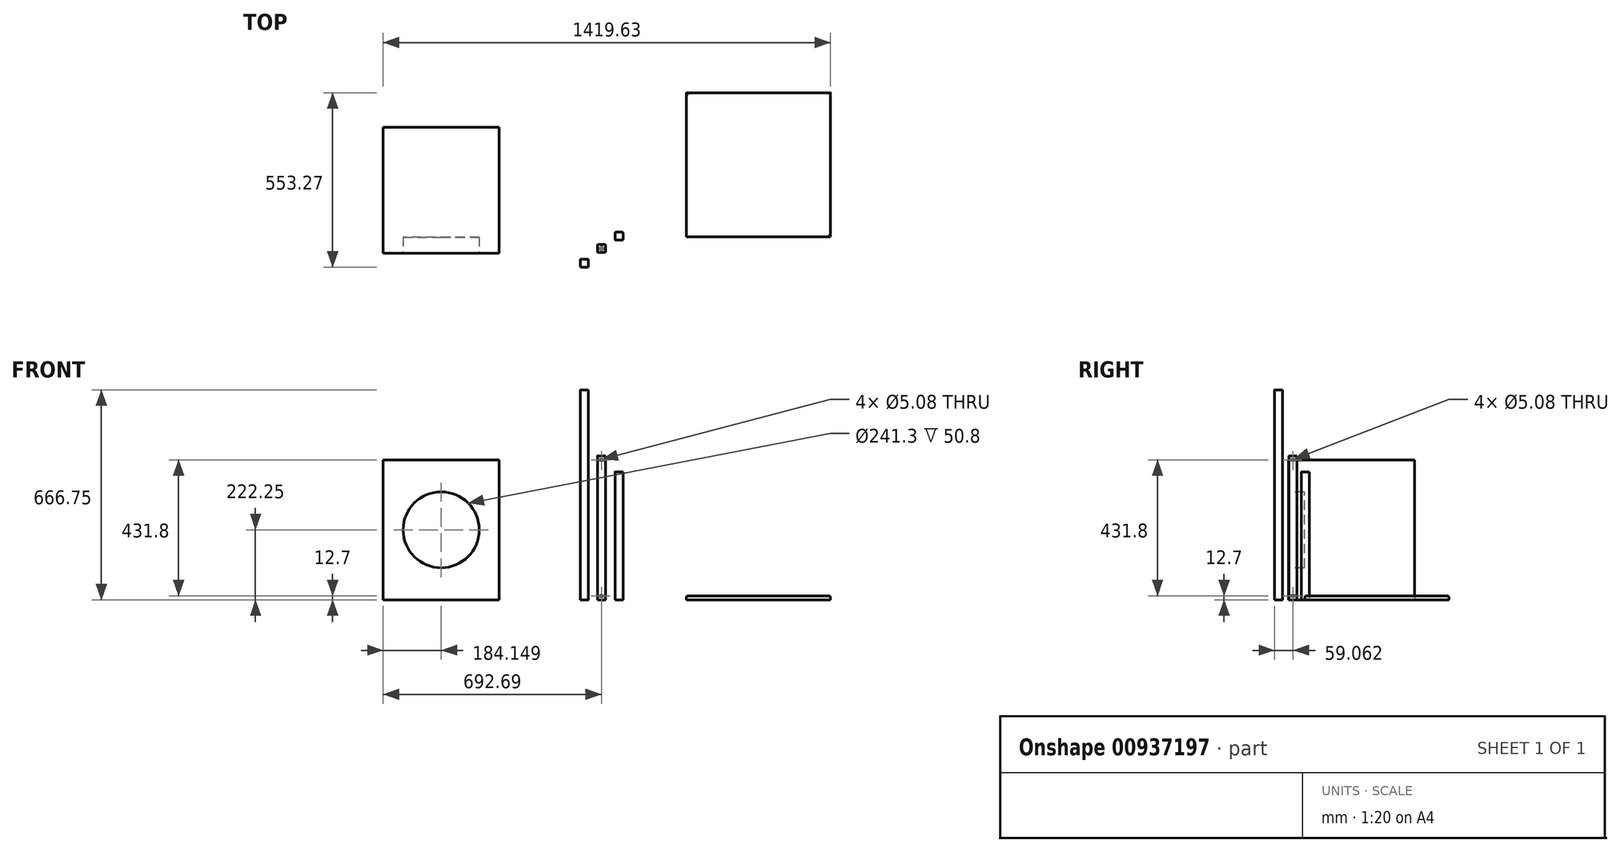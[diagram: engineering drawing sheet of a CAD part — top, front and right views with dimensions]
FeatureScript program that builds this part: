
annotation { "Feature Type Name" : "Feature", "Feature Type Description" : "" }
export const myFeature = defineFeature(function(context is Context, id is Id, definition is map)
    precondition{}
    {
        {
            var Q0;
            Q0=qCreatedBy(makeId("Top.planeOp"),FACE);
            var sketch = newSketch(context, id + "F0", { "sketchPlane" : qUnion([Q0])});
            skLineSegment(sketch, "E0.bottom", {"start": v(-525.27, 322.35) * mm, "end": v(-156.97, 322.35) * mm});
            skLineSegment(sketch, "E0.top", {"start": v(-525.27, -77.7) * mm, "end": v(-156.97, -77.7) * mm});
            skLineSegment(sketch, "E0.left", {"start": v(-525.27, 322.35) * mm, "end": v(-525.27, -77.7) * mm});
            skLineSegment(sketch, "E0.right", {"start": v(-156.97, 322.35) * mm, "end": v(-156.97, -77.7) * mm});
            skSolve(sketch);
        }
        {
            var Q0;
            Q0 = qSketchRegion(id + "F0", true);
            extrude(context, id + "F1", {"entities" : qUnion([Q0]), "depth" : 444.5 * mm, "offsetDistance" : 25.4 * mm});
        }
        {
            var Q0;
            Q0=makeQuery(id+"F1.opExtrude","SWEPT_FACE",FACE,{"disambiguationData":[OSD([sQuery(id+"F0.wireOp",EDGE,"E0.top")])]});
            var sketch = newSketch(context, id + "F2", { "sketchPlane" : qUnion([Q0])});
            skLineSegment(sketch, "E1", {"start": v(-341.12, 0) * mm, "end": v(-341.12, 222.25) * mm, "construction": true});
            skPoint(sketch, "E1.endSnap0", {"position": v(-525.27, 222.25) * mm});
            skCircle(sketch, "E2", {"center": v(-341.12, 222.25) * mm, "radius": 120.65 * mm});
            skSolve(sketch);
        }
        {
            var Q0;
            Q0 = qSketchRegion(id + "F2", true);
            extrude(context, id + "F3", {"entities" : qUnion([Q0]), "operationType" : NewBodyOperationType.REMOVE, "oppositeDirection" : true, "depth" : 50.8 * mm, "offsetDistance" : 25.4 * mm});
        }
        {
            var Q0;
            Q0=qCreatedBy(makeId("Top.planeOp"),FACE);
            var sketch = newSketch(context, id + "F4", { "sketchPlane" : qUnion([Q0])});
            skLineSegment(sketch, "E3.bottom", {"start": v(123.55, -121.85) * mm, "end": v(103.23, -121.85) * mm});
            skLineSegment(sketch, "E3.top", {"start": v(123.55, -96.45) * mm, "end": v(103.23, -96.45) * mm});
            skLineSegment(sketch, "E3.left", {"start": v(126.1, -119.3) * mm, "end": v(126.1, -98.99) * mm});
            skLineSegment(sketch, "E3.right", {"start": v(100.7, -119.3) * mm, "end": v(100.7, -98.99) * mm});
            skPoint(sketch, "E3.middle", {"position": v(113.4, -109.15) * mm});
            skPoint(sketch, "E4.visualSharp", {"position": v(100.7, -96.45) * mm});
            skArc(sketch, "E4.filletArc", {"start": v(103.23, -96.45) * mm, "mid": v(101.44, -97.2) * mm, "end": v(100.7, -98.99) * mm});
            skPoint(sketch, "E5.visualSharp", {"position": v(126.1, -96.45) * mm});
            skArc(sketch, "E5.filletArc", {"start": v(126.1, -98.99) * mm, "mid": v(125.35, -97.2) * mm, "end": v(123.55, -96.45) * mm});
            skPoint(sketch, "E6.visualSharp", {"position": v(126.1, -121.85) * mm});
            skArc(sketch, "E6.filletArc", {"start": v(123.55, -121.85) * mm, "mid": v(125.35, -121.1) * mm, "end": v(126.1, -119.3) * mm});
            skPoint(sketch, "E7.visualSharp", {"position": v(100.7, -121.85) * mm});
            skArc(sketch, "E7.filletArc", {"start": v(100.7, -119.3) * mm, "mid": v(101.44, -121.1) * mm, "end": v(103.23, -121.85) * mm});
            skSolve(sketch);
        }
        {
            var Q0;
            Q0=makeQuery(id+"F4.imprint","IMPRINT",FACE,{"disambiguationData":[TD([[makeQuery(id+"F4.imprint","IMPRINT",EDGE,{"derivedFrom":sQuery(id+"F4.wireOp",EDGE,"E3.bottom")}),-1.0]])]});
            extrude(context, id + "F5", {"entities" : qUnion([Q0]), "depth" : 666.75 * mm, "offsetDistance" : 25.4 * mm});
        }
        {
            var Q0;
            Q0=qCreatedBy(makeId("Top.planeOp"),FACE);
            var sketch = newSketch(context, id + "F6", { "sketchPlane" : qUnion([Q0])});
            skLineSegment(sketch, "E8.bottom", {"start": v(177.58, -75.49) * mm, "end": v(157.26, -75.49) * mm});
            skLineSegment(sketch, "E8.top", {"start": v(177.58, -50.09) * mm, "end": v(157.26, -50.09) * mm});
            skLineSegment(sketch, "E8.left", {"start": v(180.12, -72.95) * mm, "end": v(180.12, -52.63) * mm});
            skLineSegment(sketch, "E8.right", {"start": v(154.72, -72.95) * mm, "end": v(154.72, -52.63) * mm});
            skPoint(sketch, "E8.middle", {"position": v(167.42, -62.79) * mm});
            skPoint(sketch, "E9.visualSharp", {"position": v(154.72, -50.09) * mm});
            skArc(sketch, "E9.filletArc", {"start": v(157.26, -50.09) * mm, "mid": v(155.46, -50.83) * mm, "end": v(154.72, -52.63) * mm});
            skPoint(sketch, "E10.visualSharp", {"position": v(180.12, -50.09) * mm});
            skArc(sketch, "E10.filletArc", {"start": v(180.12, -52.63) * mm, "mid": v(179.38, -50.83) * mm, "end": v(177.58, -50.09) * mm});
            skPoint(sketch, "E11.visualSharp", {"position": v(180.12, -75.49) * mm});
            skArc(sketch, "E11.filletArc", {"start": v(177.58, -75.49) * mm, "mid": v(179.38, -74.74) * mm, "end": v(180.12, -72.95) * mm});
            skPoint(sketch, "E12.visualSharp", {"position": v(154.72, -75.49) * mm});
            skArc(sketch, "E12.filletArc", {"start": v(154.72, -72.95) * mm, "mid": v(155.46, -74.74) * mm, "end": v(157.26, -75.49) * mm});
            skSolve(sketch);
        }
        {
            var Q0;
            Q0 = qSketchRegion(id + "F6", true);
            extrude(context, id + "F7", {"entities" : qUnion([Q0]), "depth" : 457.2 * mm, "offsetDistance" : 25.4 * mm});
        }
        {
            var Q0;
            Q0=qCreatedBy(makeId("Top.planeOp"),FACE);
            var sketch = newSketch(context, id + "F8", { "sketchPlane" : qUnion([Q0])});
            skLineSegment(sketch, "E13.bottom", {"start": v(233.4, -36.5) * mm, "end": v(213.08, -36.5) * mm});
            skLineSegment(sketch, "E13.top", {"start": v(233.4, -11.1) * mm, "end": v(213.08, -11.1) * mm});
            skLineSegment(sketch, "E13.left", {"start": v(235.94, -33.97) * mm, "end": v(235.94, -13.65) * mm});
            skLineSegment(sketch, "E13.right", {"start": v(210.54, -33.97) * mm, "end": v(210.54, -13.65) * mm});
            skPoint(sketch, "E13.middle", {"position": v(223.24, -23.8) * mm});
            skPoint(sketch, "E14.visualSharp", {"position": v(210.54, -11.1) * mm});
            skArc(sketch, "E14.filletArc", {"start": v(213.08, -11.1) * mm, "mid": v(211.28, -11.85) * mm, "end": v(210.54, -13.65) * mm});
            skPoint(sketch, "E15.visualSharp", {"position": v(235.94, -11.1) * mm});
            skArc(sketch, "E15.filletArc", {"start": v(235.94, -13.65) * mm, "mid": v(235.2, -11.85) * mm, "end": v(233.4, -11.1) * mm});
            skPoint(sketch, "E16.visualSharp", {"position": v(235.94, -36.5) * mm});
            skArc(sketch, "E16.filletArc", {"start": v(233.4, -36.5) * mm, "mid": v(235.2, -35.76) * mm, "end": v(235.94, -33.97) * mm});
            skPoint(sketch, "E17.visualSharp", {"position": v(210.54, -36.5) * mm});
            skArc(sketch, "E17.filletArc", {"start": v(210.54, -33.97) * mm, "mid": v(211.28, -35.76) * mm, "end": v(213.08, -36.5) * mm});
            skSolve(sketch);
        }
        {
            var Q0;
            Q0 = qSketchRegion(id + "F8", true);
            extrude(context, id + "F9", {"entities" : qUnion([Q0]), "depth" : 406.4 * mm, "offsetDistance" : 25.4 * mm});
        }
        {
            var Q0;
            Q0=qCreatedBy(makeId("Top.planeOp"),FACE);
            var sketch = newSketch(context, id + "F10", { "sketchPlane" : qUnion([Q0])});
            skLineSegment(sketch, "E18.bottom", {"start": v(894.36, -25.78) * mm, "end": v(437.16, -25.78) * mm});
            skLineSegment(sketch, "E18.top", {"start": v(894.36, 431.42) * mm, "end": v(437.16, 431.42) * mm});
            skLineSegment(sketch, "E18.left", {"start": v(894.36, -25.78) * mm, "end": v(894.36, 431.42) * mm});
            skLineSegment(sketch, "E18.right", {"start": v(437.16, -25.78) * mm, "end": v(437.16, 431.42) * mm});
            skPoint(sketch, "E18.middle", {"position": v(665.76, 202.82) * mm});
            skSolve(sketch);
        }
        {
            var Q0;
            Q0 = qSketchRegion(id + "F10", true);
            extrude(context, id + "F11", {"entities" : qUnion([Q0]), "depth" : 12.7 * mm, "offsetDistance" : 25.4 * mm});
        }
        {
            var Q0;
            Q0=makeQuery(id+"F11.opExtrude","CAP_FACE",FACE,{"disambiguationData":[OSD([sQuery(id+"F10.wireOp",EDGE,"E18.bottom"),sQuery(id+"F10.wireOp",EDGE,"E18.top"),sQuery(id+"F10.wireOp",EDGE,"E18.left"),sQuery(id+"F10.wireOp",EDGE,"E18.right")])],"isStart":false});
            fillet(context, id + "F12", {"entities" : qUnion([Q0]), "radius" : 5.08 * mm, "tangentPropagation" : true, "allowEdgeOverflow" : false});
        }
        {
            var Q0;
            Q0=makeQuery(id+"F7.opExtrude","SWEPT_FACE",FACE,{"disambiguationData":[OSD([sQuery(id+"F6.wireOp",EDGE,"E8.bottom")])]});
            var sketch = newSketch(context, id + "F13", { "sketchPlane" : qUnion([Q0])});
            skLineSegment(sketch, "E19", {"start": v(167.42, 457.2) * mm, "end": v(167.42, 444.5) * mm, "construction": true});
            skLineSegment(sketch, "E20", {"start": v(167.42, 0) * mm, "end": v(167.42, 12.7) * mm, "construction": true});
            skCircle(sketch, "E21", {"center": v(167.42, 12.7) * mm, "radius": 2.54 * mm});
            skCircle(sketch, "E22", {"center": v(167.42, 444.5) * mm, "radius": 2.54 * mm});
            skSolve(sketch);
        }
        {
            var Q0;
            Q0 = qSketchRegion(id + "F13", true);
            extrude(context, id + "F14", {"entities" : qUnion([Q0]), "operationType" : NewBodyOperationType.REMOVE, "oppositeDirection" : true, "depth" : 25.4 * mm, "offsetDistance" : 25.4 * mm});
        }
        {
            var Q0;
            Q0=makeQuery(id+"F7.opExtrude","SWEPT_FACE",FACE,{"disambiguationData":[OSD([sQuery(id+"F6.wireOp",EDGE,"E8.left")])]});
            var sketch = newSketch(context, id + "F15", { "sketchPlane" : qUnion([Q0])});
            skLineSegment(sketch, "E23", {"start": v(-62.79, 457.2) * mm, "end": v(-62.79, 444.5) * mm, "construction": true});
            skLineSegment(sketch, "E24", {"start": v(-62.79, 0) * mm, "end": v(-62.79, 12.7) * mm, "construction": true});
            skCircle(sketch, "E25", {"center": v(-62.79, 12.7) * mm, "radius": 2.54 * mm});
            skCircle(sketch, "E26", {"center": v(-62.79, 444.5) * mm, "radius": 2.54 * mm});
            skSolve(sketch);
        }
        {
            var Q0;
            Q0 = qSketchRegion(id + "F15", true);
            extrude(context, id + "F16", {"entities" : qUnion([Q0]), "operationType" : NewBodyOperationType.REMOVE, "oppositeDirection" : true, "depth" : 25.4 * mm, "offsetDistance" : 25.4 * mm});
        }
    });
